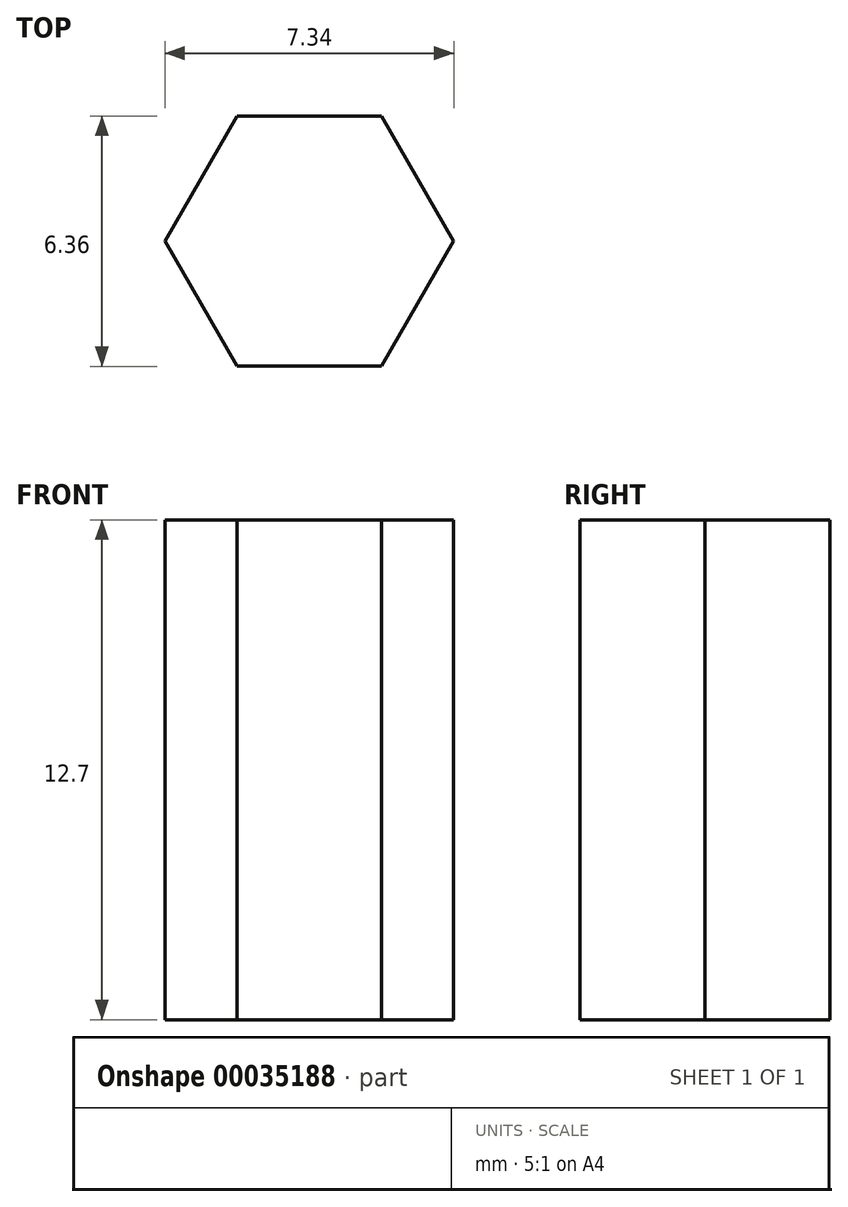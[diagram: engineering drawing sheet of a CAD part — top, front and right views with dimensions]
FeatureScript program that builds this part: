
annotation { "Feature Type Name" : "Feature", "Feature Type Description" : "" }
export const myFeature = defineFeature(function(context is Context, id is Id, definition is map)
    precondition{}
    {
        {
            var Q0;
            Q0=qCreatedBy(makeId("Top.planeOp"),FACE);
            var sketch = newSketch(context, id + "F0", { "sketchPlane" : qUnion([Q0])});
            skLineSegment(sketch, "E0", {"start": v(0, 0) * mm, "end": v(93.48, 0) * mm, "construction": true});
            skLineSegment(sketch, "E1.0", {"start": v(0, -3.18) * mm, "end": v(93.48, -3.18) * mm, "construction": true});
            skLineSegment(sketch, "E2.0", {"start": v(0, 3.18) * mm, "end": v(93.48, 3.18) * mm, "construction": true});
            skCircle(sketch, "E3.cCircle", {"center": v(0, 0) * mm, "radius": 3.18 * mm, "construction": true});
            skLineSegment(sketch, "E3.0", {"start": v(-1.83, 3.18) * mm, "end": v(1.83, 3.18) * mm});
            skLineSegment(sketch, "E3.1", {"start": v(1.83, 3.18) * mm, "end": v(3.67, 0) * mm});
            skLineSegment(sketch, "E3.2", {"start": v(3.67, 0) * mm, "end": v(1.83, -3.17) * mm});
            skLineSegment(sketch, "E3.3", {"start": v(1.83, -3.17) * mm, "end": v(-1.83, -3.18) * mm});
            skLineSegment(sketch, "E3.4", {"start": v(-1.83, -3.18) * mm, "end": v(-3.67, 0) * mm});
            skLineSegment(sketch, "E3.5", {"start": v(-3.67, 0) * mm, "end": v(-1.83, 3.17) * mm});
            skPoint(sketch, "E3.0.midPoint", {"position": v(0, 3.18) * mm});
            skSolve(sketch);
        }
        {
            var Q0;
            Q0=makeQuery(id+"F0.imprint","IMPRINT",FACE,{"disambiguationData":[TD([[makeQuery(id+"F0.imprint","IMPRINT",EDGE,{"derivedFrom":sQuery(id+"F0.wireOp",EDGE,"E3.0")}),-1.0]])]});
            extrude(context, id + "F1", {"entities" : qUnion([Q0]), "depth" : 12.7 * mm});
        }
    });
